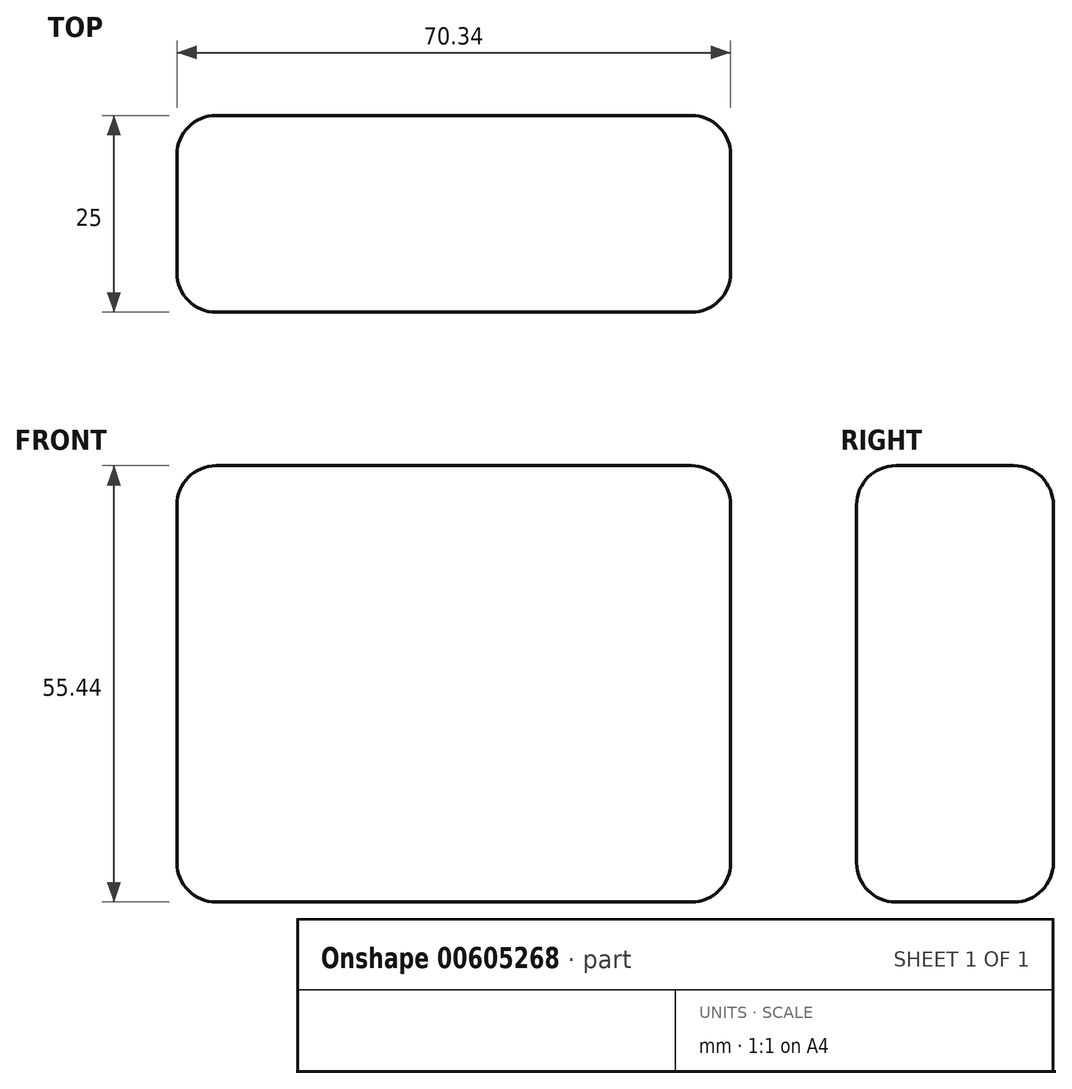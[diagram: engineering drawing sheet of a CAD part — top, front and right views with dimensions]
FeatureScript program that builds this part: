
annotation { "Feature Type Name" : "Feature", "Feature Type Description" : "" }
export const myFeature = defineFeature(function(context is Context, id is Id, definition is map)
    precondition{}
    {
        {
            var Q0;
            Q0=qCreatedBy(makeId("Front.planeOp"),FACE);
            var sketch = newSketch(context, id + "F0", { "sketchPlane" : qUnion([Q0])});
            skLineSegment(sketch, "E0.bottom", {"start": v(-49.6, 23.78) * mm, "end": v(20.74, 23.78) * mm});
            skLineSegment(sketch, "E0.top", {"start": v(-49.6, -31.66) * mm, "end": v(20.74, -31.66) * mm});
            skLineSegment(sketch, "E0.left", {"start": v(-49.6, 23.78) * mm, "end": v(-49.6, -31.66) * mm});
            skLineSegment(sketch, "E0.right", {"start": v(20.74, 23.78) * mm, "end": v(20.74, -31.66) * mm});
            skSolve(sketch);
        }
        {
            var Q0;
            Q0 = qSketchRegion(id + "F0", true);
            extrude(context, id + "F1", {"entities" : qUnion([Q0]), "depth" : 25 * mm, "offsetDistance" : 25 * mm});
        }
        {
            var Q0;
            Q0=makeQuery(id+"F1.opExtrude","SWEPT_EDGE",EDGE,{"disambiguationData":[OSD([sQuery(id+"F0.wireOp",EDGE,"E0.bottom"),sQuery(id+"F0.wireOp",EDGE,"E0.left")])]});
            var Q1;
            Q1=makeQuery(id+"F1.opExtrude","SWEPT_FACE",FACE,{"disambiguationData":[OSD([sQuery(id+"F0.wireOp",EDGE,"E0.bottom")])]});
            var Q2;
            Q2=makeQuery(id+"F1.opExtrude","SWEPT_EDGE",EDGE,{"disambiguationData":[OSD([sQuery(id+"F0.wireOp",EDGE,"E0.bottom"),sQuery(id+"F0.wireOp",EDGE,"E0.right")])]});
            var Q3;
            Q3=makeQuery(id+"F1.opExtrude","CAP_FACE",FACE,{"disambiguationData":[OSD([sQuery(id+"F0.wireOp",EDGE,"E0.bottom"),sQuery(id+"F0.wireOp",EDGE,"E0.top"),sQuery(id+"F0.wireOp",EDGE,"E0.left"),sQuery(id+"F0.wireOp",EDGE,"E0.right")])],"isStart":true});
            var Q4;
            Q4=makeQuery(id+"F1.opExtrude","CAP_FACE",FACE,{"disambiguationData":[OSD([sQuery(id+"F0.wireOp",EDGE,"E0.bottom"),sQuery(id+"F0.wireOp",EDGE,"E0.top"),sQuery(id+"F0.wireOp",EDGE,"E0.left"),sQuery(id+"F0.wireOp",EDGE,"E0.right")])],"isStart":false});
            var Q5;
            Q5=makeQuery(id+"F1.opExtrude","SWEPT_EDGE",EDGE,{"disambiguationData":[OSD([sQuery(id+"F0.wireOp",EDGE,"E0.top"),sQuery(id+"F0.wireOp",EDGE,"E0.right")])]});
            var Q6;
            Q6=makeQuery(id+"F1.opExtrude","SWEPT_FACE",FACE,{"disambiguationData":[OSD([sQuery(id+"F0.wireOp",EDGE,"E0.top")])]});
            var Q7;
            Q7=makeQuery(id+"F1.opExtrude","CAP_EDGE",EDGE,{"disambiguationData":[OSD([sQuery(id+"F0.wireOp",EDGE,"E0.bottom")])],"isStart":true});
            var Q8;
            Q8=makeQuery(id+"F1.opExtrude","CAP_EDGE",EDGE,{"disambiguationData":[OSD([sQuery(id+"F0.wireOp",EDGE,"E0.bottom")])],"isStart":false});
            var Q9;
            Q9=makeQuery(id+"F1.opExtrude","SWEPT_FACE",FACE,{"disambiguationData":[OSD([sQuery(id+"F0.wireOp",EDGE,"E0.right")])]});
            var Q10;
            Q10=makeQuery(id+"F1.opExtrude","CAP_EDGE",EDGE,{"disambiguationData":[OSD([sQuery(id+"F0.wireOp",EDGE,"E0.top")])],"isStart":false});
            var Q11;
            Q11=makeQuery(id+"F1.opExtrude","SWEPT_EDGE",EDGE,{"disambiguationData":[OSD([sQuery(id+"F0.wireOp",EDGE,"E0.top"),sQuery(id+"F0.wireOp",EDGE,"E0.left")])]});
            var Q12;
            Q12=makeQuery(id+"F1.opExtrude","SWEPT_FACE",FACE,{"disambiguationData":[OSD([sQuery(id+"F0.wireOp",EDGE,"E0.left")])]});
            var Q13;
            Q13=makeQuery(id+"F1.opExtrude","CAP_EDGE",EDGE,{"disambiguationData":[OSD([sQuery(id+"F0.wireOp",EDGE,"E0.top")])],"isStart":true});
            var Q14;
            Q14=makeQuery(id+"F1.opExtrude","CAP_EDGE",EDGE,{"disambiguationData":[OSD([sQuery(id+"F0.wireOp",EDGE,"E0.left")])],"isStart":true});
            var Q15;
            Q15=makeQuery(id+"F1.opExtrude","CAP_EDGE",EDGE,{"disambiguationData":[OSD([sQuery(id+"F0.wireOp",EDGE,"E0.left")])],"isStart":false});
            var Q16;
            Q16=makeQuery(id+"F1.opExtrude","CAP_EDGE",EDGE,{"disambiguationData":[OSD([sQuery(id+"F0.wireOp",EDGE,"E0.right")])],"isStart":true});
            var Q17;
            Q17=makeQuery(id+"F1.opExtrude","CAP_EDGE",EDGE,{"disambiguationData":[OSD([sQuery(id+"F0.wireOp",EDGE,"E0.right")])],"isStart":false});
            fillet(context, id + "F2", {"entities" : qUnion([Q0, Q1, Q2, Q3, Q4, Q5, Q6, Q7, Q8, Q9, Q10, Q11, Q12, Q13, Q14, Q15, Q16, Q17]), "radius" : 5 * mm, "tangentPropagation" : true, "allowEdgeOverflow" : false});
        }
    });
